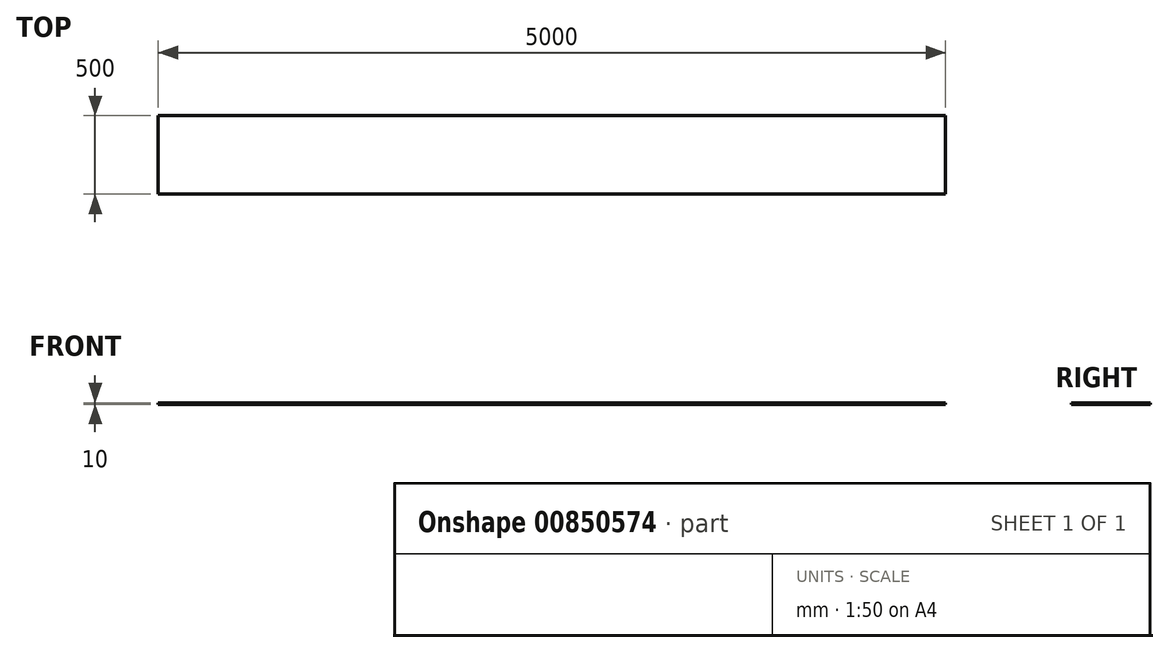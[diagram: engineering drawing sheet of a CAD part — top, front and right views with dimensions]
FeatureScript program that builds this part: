
annotation { "Feature Type Name" : "Feature", "Feature Type Description" : "" }
export const myFeature = defineFeature(function(context is Context, id is Id, definition is map)
    precondition{}
    {
        {
            var Q0;
            Q0=qCreatedBy(makeId("Top.planeOp"),FACE);
            var sketch = newSketch(context, id + "F0", { "sketchPlane" : qUnion([Q0])});
            skLineSegment(sketch, "E0.bottom", {"start": v(-2500, 250) * mm, "end": v(2500, 250) * mm});
            skLineSegment(sketch, "E0.top", {"start": v(-2500, -250) * mm, "end": v(2500, -250) * mm});
            skLineSegment(sketch, "E0.left", {"start": v(-2500, 250) * mm, "end": v(-2500, -250) * mm});
            skLineSegment(sketch, "E0.right", {"start": v(2500, 250) * mm, "end": v(2500, -250) * mm});
            skSolve(sketch);
        }
        {
            var Q0;
            Q0=makeQuery(id+"F0.imprint","IMPRINT",FACE,{"disambiguationData":[TD([[makeQuery(id+"F0.imprint","IMPRINT",EDGE,{"derivedFrom":sQuery(id+"F0.wireOp",EDGE,"E0.bottom")}),-1.0]])]});
            extrude(context, id + "F1", {"entities" : qUnion([Q0]), "depth" : 10 * mm, "offsetDistance" : 25 * mm});
        }
    });
